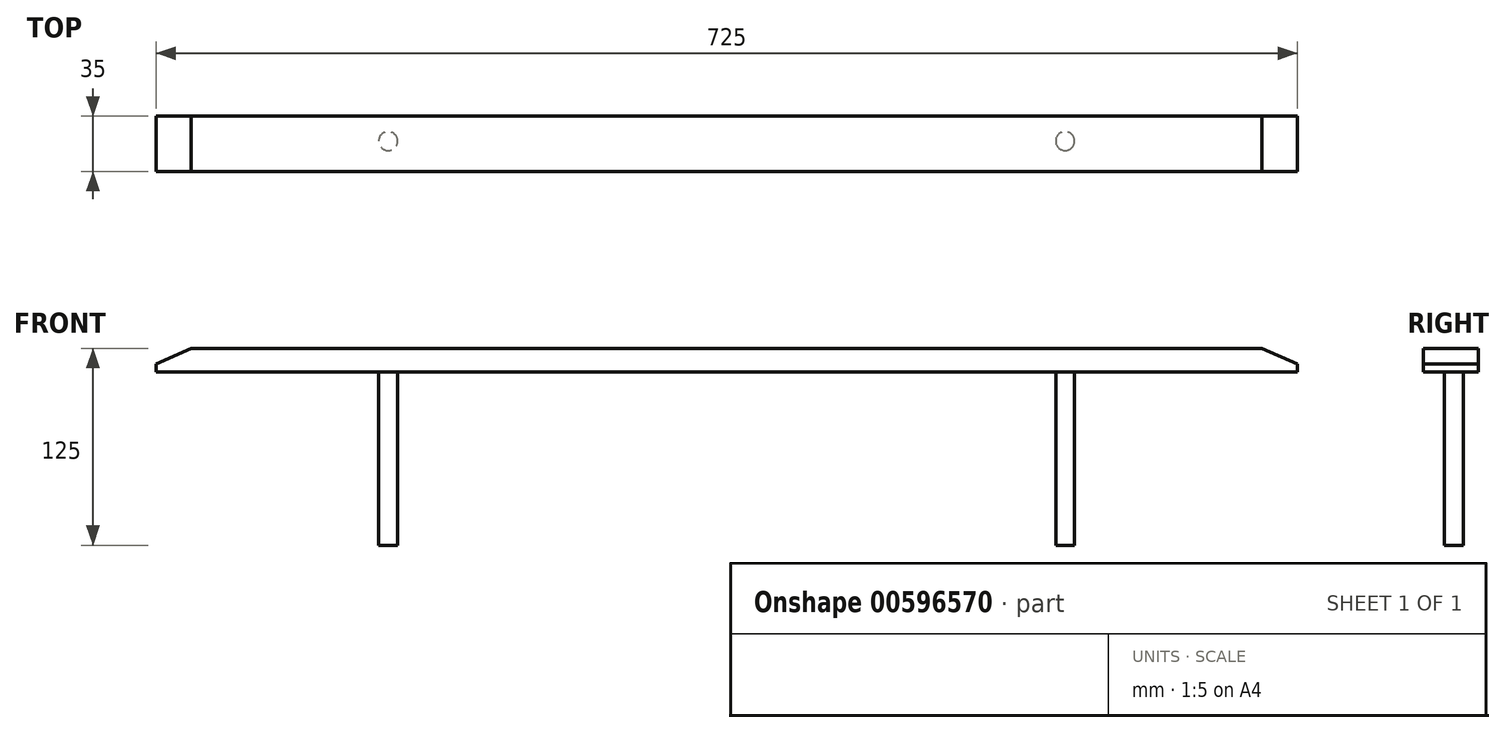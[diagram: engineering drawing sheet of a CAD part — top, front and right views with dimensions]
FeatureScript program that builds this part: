
annotation { "Feature Type Name" : "Feature", "Feature Type Description" : "" }
export const myFeature = defineFeature(function(context is Context, id is Id, definition is map)
    precondition{}
    {
        {
            var Q0;
            Q0=qCreatedBy(makeId("Front.planeOp"),FACE);
            var sketch = newSketch(context, id + "F0", { "sketchPlane" : qUnion([Q0])});
            skLineSegment(sketch, "E0", {"start": v(22.5, 0) * mm, "end": v(702.5, 0) * mm});
            skLineSegment(sketch, "E1.0", {"start": v(0, -15) * mm, "end": v(725, -15) * mm});
            skLineSegment(sketch, "E2", {"start": v(0, 0) * mm, "end": v(0, 41.37) * mm, "construction": true});
            skLineSegment(sketch, "E3.0", {"start": v(22.5, -22.28) * mm, "end": v(22.5, 41.37) * mm, "construction": true});
            skLineSegment(sketch, "E4", {"start": v(0, -10) * mm, "end": v(22.5, 0) * mm});
            skLineSegment(sketch, "E5", {"start": v(0, -15) * mm, "end": v(0, -10) * mm});
            skLineSegment(sketch, "E6", {"start": v(362.5, -15) * mm, "end": v(362.5, 24.31) * mm, "construction": true});
            skLineSegment(sketch, "E7.MirrorCS", {"start": v(725, -10) * mm, "end": v(702.5, 0) * mm});
            skLineSegment(sketch, "E8.MirrorCS", {"start": v(725, -15) * mm, "end": v(725, -10) * mm});
            skSolve(sketch);
        }
        {
            var Q0;
            Q0=makeQuery(id+"F0.imprint","IMPRINT",FACE,{"disambiguationData":[TD([[makeQuery(id+"F0.imprint","IMPRINT",EDGE,{"derivedFrom":sQuery(id+"F0.wireOp",EDGE,"E0")}),-1.0]])]});
            extrude(context, id + "F1", {"entities" : qUnion([Q0]), "depth" : 35 * mm, "offsetDistance" : 25 * mm});
        }
        {
            var Q0;
            Q0=makeQuery(id+"F1.opExtrude","SWEPT_FACE",FACE,{"disambiguationData":[OSD([sQuery(id+"F0.wireOp",EDGE,"E1.0")])]});
            var sketch = newSketch(context, id + "F2", { "sketchPlane" : qUnion([Q0])});
            skCircle(sketch, "E9", {"center": v(147.5, 15.75) * mm, "radius": 6 * mm});
            skLineSegment(sketch, "E10", {"start": v(362.5, 35) * mm, "end": v(362.5, 0) * mm, "construction": true});
            skCircle(sketch, "E11.MirrorC", {"center": v(577.5, 15.75) * mm, "radius": 6 * mm});
            skSolve(sketch);
        }
        {
            var Q0;
            Q0 = qSketchRegion(id + "F2", true);
            extrude(context, id + "F3", {"entities" : qUnion([Q0]), "operationType" : NewBodyOperationType.ADD, "depth" : 110 * mm, "offsetDistance" : 25 * mm});
        }
    });
